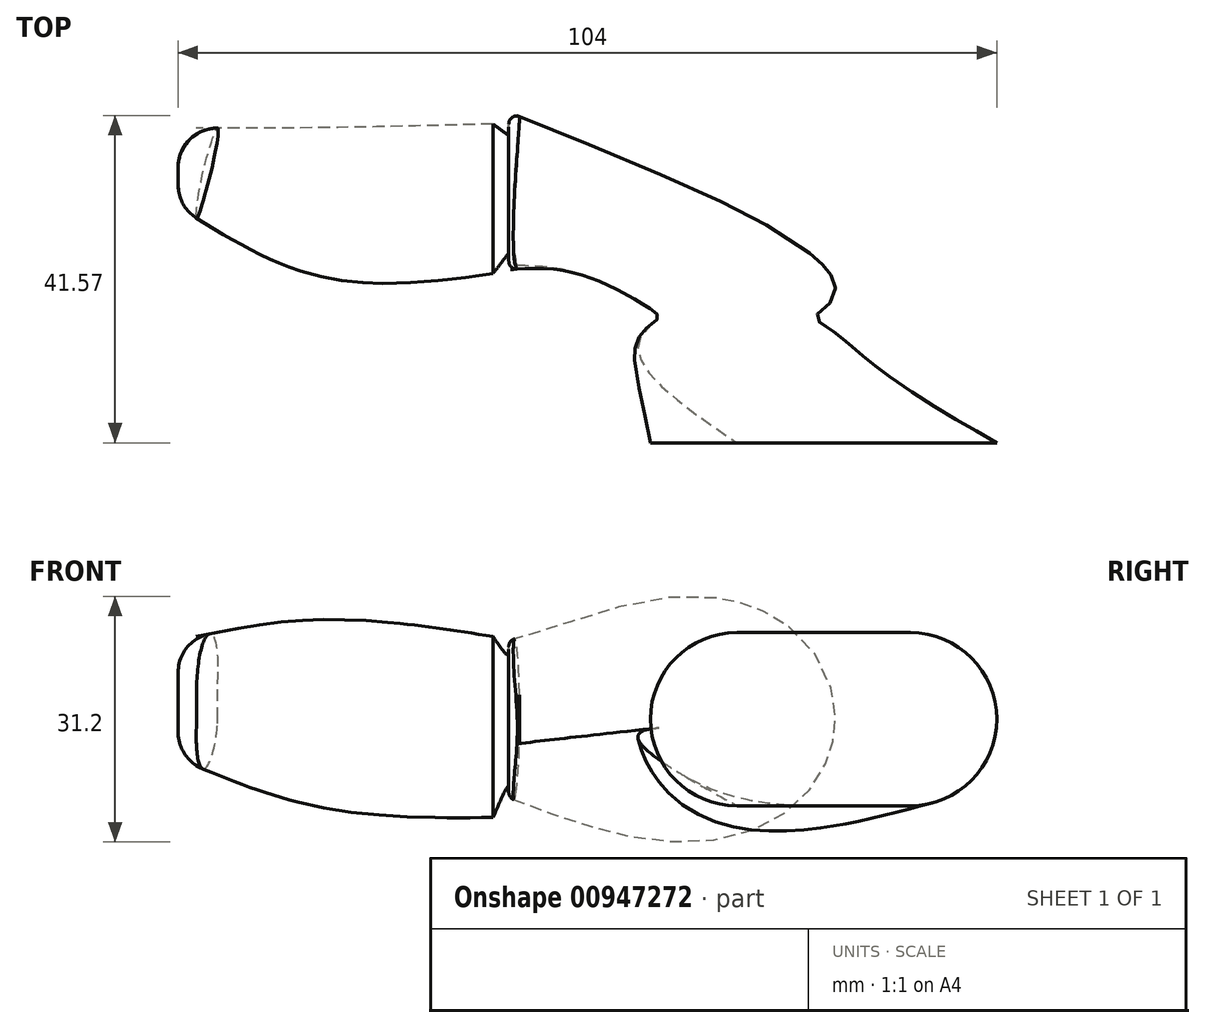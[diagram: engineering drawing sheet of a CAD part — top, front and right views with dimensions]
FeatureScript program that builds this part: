
annotation { "Feature Type Name" : "Feature", "Feature Type Description" : "" }
export const myFeature = defineFeature(function(context is Context, id is Id, definition is map)
    precondition{}
    {
        {
            var Q0;
            Q0=qCreatedBy(makeId("Front.planeOp"),FACE);
            cPlane(context, id + "F0", {"entities" : qUnion([Q0]), "cplaneType" : CPlaneType.OFFSET, "offset" : 15 * mm, "oppositeDirection" : true, "width" : 150 * mm, "height" : 150 * mm});
        }
        {
            var Q0;
            Q0=qCreatedBy(makeId("Front.planeOp"),FACE);
            var sketch = newSketch(context, id + "F1", { "sketchPlane" : qUnion([Q0])});
            skArc(sketch, "E0", {"start": v(11, -11) * mm, "mid": v(22, 0) * mm, "end": v(11, 11) * mm});
            skLineSegment(sketch, "E1", {"start": v(0, 30.33) * mm, "end": v(0, -39.22) * mm, "construction": true});
            skArc(sketch, "E2.MirrorC", {"start": v(-11, -11) * mm, "mid": v(-22, 0) * mm, "end": v(-11, 11) * mm});
            skLineSegment(sketch, "E3", {"start": v(11, 11) * mm, "end": v(-11, 11) * mm});
            skLineSegment(sketch, "E4", {"start": v(11, -11) * mm, "end": v(-11, -11) * mm});
            skSolve(sketch);
        }
        {
            var Q0;
            Q0=qCreatedBy(id+"F0.planeOp",FACE);
            var sketch = newSketch(context, id + "F2", { "sketchPlane" : qUnion([Q0])});
            skCircle(sketch, "E5", {"center": v(-11, 0) * mm, "radius": 11 * mm});
            skSolve(sketch);
        }
        {
            var Q0;
            Q0=qCreatedBy(id+"F0.planeOp",FACE);
            cPlane(context, id + "F3", {"entities" : qUnion([Q0]), "cplaneType" : CPlaneType.OFFSET, "offset" : 1 * mm, "oppositeDirection" : true, "width" : 150 * mm, "height" : 150 * mm});
        }
        {
            var Q0;
            Q0=qCreatedBy(id+"F3.planeOp",FACE);
            var sketch = newSketch(context, id + "F4", { "sketchPlane" : qUnion([Q0])});
            skCircle(sketch, "E6", {"center": v(-11, 0) * mm, "radius": 10 * mm});
            skSolve(sketch);
        }
        {
            var Q0;
            Q0=qCreatedBy(id+"F3.planeOp",FACE);
            cPlane(context, id + "F5", {"entities" : qUnion([Q0]), "cplaneType" : CPlaneType.OFFSET, "offset" : 1 * mm, "oppositeDirection" : true, "width" : 150 * mm, "height" : 150 * mm});
        }
        {
            var Q0;
            Q0=qCreatedBy(id+"F5.planeOp",FACE);
            var sketch = newSketch(context, id + "F6", { "sketchPlane" : qUnion([Q0])});
            skCircle(sketch, "E7", {"center": v(-11, 0) * mm, "radius": 11 * mm});
            skSolve(sketch);
        }
        {
            var Q0;
            Q0=qCreatedBy(makeId("Right.planeOp"),FACE);
            cPlane(context, id + "F7", {"entities" : qUnion([Q0]), "cplaneType" : CPlaneType.OFFSET, "offset" : 40 * mm, "oppositeDirection" : true, "width" : 150 * mm, "height" : 150 * mm});
        }
        {
            var Q0;
            Q0=qCreatedBy(id+"F7.planeOp",FACE);
            var sketch = newSketch(context, id + "F8", { "sketchPlane" : qUnion([Q0])});
            skCircle(sketch, "E8", {"center": v(32, 0) * mm, "radius": 10 * mm});
            skSolve(sketch);
        }
        {
            var Q0;
            Q0=makeQuery(id+"F8.imprint","IMPRINT",FACE,{"disambiguationData":[TD([[makeQuery(id+"F8.imprint","IMPRINT",EDGE,{"derivedFrom":sQuery(id+"F8.wireOp",EDGE,"E8")}),1.0]])]});
            var Q1;
            Q1=makeQuery(id+"F6.imprint","IMPRINT",FACE,{"disambiguationData":[TD([[makeQuery(id+"F6.imprint","IMPRINT",EDGE,{"derivedFrom":sQuery(id+"F6.wireOp",EDGE,"E7")}),1.0]])]});
            var Q2;
            Q2=makeQuery(id+"F4.imprint","IMPRINT",FACE,{"disambiguationData":[TD([[makeQuery(id+"F4.imprint","IMPRINT",EDGE,{"derivedFrom":sQuery(id+"F4.wireOp",EDGE,"E6")}),1.0]])]});
            var Q3;
            Q3=makeQuery(id+"F2.imprint","IMPRINT",FACE,{"disambiguationData":[TD([[makeQuery(id+"F2.imprint","IMPRINT",EDGE,{"derivedFrom":sQuery(id+"F2.wireOp",EDGE,"E5")}),1.0]])]});
            var Q4;
            Q4=makeQuery(id+"F1.imprint","IMPRINT",FACE,{"disambiguationData":[TD([[makeQuery(id+"F1.imprint","IMPRINT",EDGE,{"derivedFrom":sQuery(id+"F1.wireOp",EDGE,"E0")}),1.0]])]});
            loft(context, id + "F9", {"sheetProfilesArray" : [{ "sheetProfileEntities" : qUnion([Q0]) }, { "sheetProfileEntities" : qUnion([Q1]) }, { "sheetProfileEntities" : qUnion([Q2]) }, { "sheetProfileEntities" : qUnion([Q3]) }, { "sheetProfileEntities" : qUnion([Q4]) }]});
        }
        {
            var Q0;
            Q0=makeQuery(id+"F9.opLoft","CAP_FACE",FACE,{"disambiguationData":[OSD([makeQuery(id+"F8.imprint","IMPRINT",FACE,{"disambiguationData":[TD([[makeQuery(id+"F8.imprint","IMPRINT",EDGE,{"derivedFrom":sQuery(id+"F8.wireOp",EDGE,"E8")}),1.0]])]})])],"isStart":true});
            fillet(context, id + "F10", {"entities" : qUnion([Q0]), "tangentPropagation" : true, "radius" : 1 * mm, "defaultsChanged" : true, "vertexSettings" : [], "allowEdgeOverflow" : false});
        }
        {
            var Q0;
            Q0=makeQuery(id+"F9.opLoft","CAP_FACE",FACE,{"disambiguationData":[OSD([makeQuery(id+"F8.imprint","IMPRINT",FACE,{"disambiguationData":[TD([[makeQuery(id+"F8.imprint","IMPRINT",EDGE,{"derivedFrom":sQuery(id+"F8.wireOp",EDGE,"E8")}),1.0]])]})])],"isStart":true});
            var sketch = newSketch(context, id + "F11", { "sketchPlane" : qUnion([Q0])});
            skFitSpline(sketch, "E9.0", {"points": [v(-29.1, 8.18) * mm, v(-29.6, 8.33) * mm, v(-30.63, 8.52) * mm, v(-31.94, 8.48) * mm, v(-32.97, 8.27) * mm, v(-33.7, 8.04) * mm, v(-34.42, 7.73) * mm, v(-35.1, 7.35) * mm, v(-35.74, 6.9) * mm, v(-36.33, 6.4) * mm, v(-36.87, 5.82) * mm, v(-37.35, 5.21) * mm, v(-37.78, 4.56) * mm, v(-38.14, 3.88) * mm, v(-38.45, 3.15) * mm, v(-38.62, 2.66) * mm, v(-38.69, 2.4) * mm]});
            skFitSpline(sketch, "E9.1", {"points": [v(-38.69, 2.4) * mm, v(-38.83, 1.92) * mm, v(-38.97, 1.18) * mm, v(-39.04, 0.18) * mm, v(-39.04, -0.59) * mm, v(-38.97, -1.34) * mm, v(-38.85, -2.08) * mm, v(-38.66, -2.8) * mm, v(-38.41, -3.53) * mm, v(-38.1, -4.22) * mm, v(-37.75, -4.87) * mm, v(-37.33, -5.5) * mm, v(-36.85, -6.09) * mm, v(-36.32, -6.63) * mm, v(-35.56, -7.28) * mm, v(-34.92, -7.68) * mm, v(-34.46, -7.9) * mm]});
            skFitSpline(sketch, "E9.2", {"points": [v(-34.46, -7.9) * mm, v(-33.97, -8.13) * mm, v(-33.21, -8.4) * mm, v(-32.14, -8.58) * mm, v(-31.33, -8.62) * mm, v(-30.52, -8.57) * mm, v(-29.72, -8.43) * mm, v(-28.94, -8.2) * mm, v(-28.2, -7.88) * mm, v(-27.61, -7.54) * mm, v(-27.17, -7.22) * mm, v(-26.75, -6.88) * mm, v(-26.36, -6.5) * mm, v(-26.02, -6.09) * mm, v(-25.7, -5.65) * mm, v(-25.35, -5.06) * mm, v(-25.02, -4.33) * mm, v(-24.75, -3.56) * mm, v(-24.61, -3.03) * mm, v(-24.55, -2.77) * mm]});
            skFitSpline(sketch, "E9.3", {"points": [v(-24.55, -2.77) * mm, v(-24.42, -2.23) * mm, v(-24.24, -1.14) * mm, v(-24.13, 0.23) * mm, v(-24.12, 1.33) * mm, v(-24.18, 2.44) * mm, v(-24.37, 3.52) * mm, v(-24.77, 4.57) * mm, v(-25.17, 5.29) * mm, v(-25.66, 5.95) * mm, v(-26.24, 6.56) * mm, v(-26.87, 7.09) * mm, v(-27.57, 7.54) * mm, v(-28.32, 7.91) * mm, v(-28.84, 8.1) * mm, v(-29.1, 8.18) * mm]});
            skSolve(sketch);
        }
        {
            var Q0;
            Q0=qCreatedBy(id+"F7.planeOp",FACE);
            cPlane(context, id + "F12", {"entities" : qUnion([Q0]), "cplaneType" : CPlaneType.OFFSET, "offset" : 2 * mm, "oppositeDirection" : true, "width" : 150 * mm, "height" : 150 * mm});
        }
        {
            var Q0;
            Q0=qCreatedBy(id+"F12.planeOp",FACE);
            var sketch = newSketch(context, id + "F13", { "sketchPlane" : qUnion([Q0])});
            skArc(sketch, "E10", {"start": v(21.5, -3) * mm, "mid": v(31, -12.5) * mm, "end": v(40.5, -3) * mm});
            skArc(sketch, "E11", {"start": v(40.5, 1) * mm, "mid": v(31, 10.5) * mm, "end": v(21.5, 1) * mm});
            skLineSegment(sketch, "E12", {"start": v(40.5, 1) * mm, "end": v(40.5, -3) * mm});
            skLineSegment(sketch, "E13", {"start": v(21.5, -3) * mm, "end": v(21.5, 1) * mm});
            skSolve(sketch);
        }
        {
            var Q0;
            Q0 = qSketchRegion(id + "F11", true);
            var Q1;
            Q1 = qSketchRegion(id + "F13", true);
            loft(context, id + "F14", {"operationType" : NewBodyOperationType.ADD, "sheetProfilesArray" : [{ "sheetProfileEntities" : qUnion([Q0]) }, { "sheetProfileEntities" : qUnion([Q1]) }]});
        }
        {
            var Q0;
            Q0=makeQuery(id+"F13.imprint","IMPRINT",FACE,{"disambiguationData":[TD([[makeQuery(id+"F13.imprint","IMPRINT",EDGE,{"derivedFrom":sQuery(id+"F13.wireOp",EDGE,"E10")}),1.0]])]});
            var sketch = newSketch(context, id + "F15", { "sketchPlane" : qUnion([Q0])});
            skArc(sketch, "E14.0", {"start": v(40.5, 1) * mm, "mid": v(31, 10.5) * mm, "end": v(21.5, 1) * mm});
            skArc(sketch, "E14.1", {"start": v(21.5, -3) * mm, "mid": v(31, -12.5) * mm, "end": v(40.5, -3) * mm});
            skLineSegment(sketch, "E14.2", {"start": v(21.5, -3) * mm, "end": v(21.5, 1) * mm});
            skLineSegment(sketch, "E14.3", {"start": v(40.5, 1) * mm, "end": v(40.5, -3) * mm});
            skSolve(sketch);
        }
        {
            var Q0;
            Q0=qCreatedBy(id+"F12.planeOp",FACE);
            cPlane(context, id + "F16", {"entities" : qUnion([Q0]), "cplaneType" : CPlaneType.OFFSET, "offset" : 25 * mm, "oppositeDirection" : true, "width" : 150 * mm, "height" : 150 * mm});
        }
        {
            var Q0;
            Q0=qCreatedBy(id+"F16.planeOp",FACE);
            var sketch = newSketch(context, id + "F17", { "sketchPlane" : qUnion([Q0])});
            skArc(sketch, "E15", {"start": v(40, 3.5) * mm, "mid": v(31, 12.5) * mm, "end": v(22, 3.5) * mm});
            skArc(sketch, "E16", {"start": v(22, -1.5) * mm, "mid": v(31, -10.5) * mm, "end": v(40, -1.5) * mm});
            skLineSegment(sketch, "E17", {"start": v(40, -1.5) * mm, "end": v(40, 3.5) * mm});
            skLineSegment(sketch, "E18", {"start": v(22, -1.5) * mm, "end": v(22, 3.5) * mm});
            skSolve(sketch);
        }
        {
            var Q0;
            Q0=qCreatedBy(id+"F16.planeOp",FACE);
            cPlane(context, id + "F18", {"entities" : qUnion([Q0]), "cplaneType" : CPlaneType.OFFSET, "offset" : 15 * mm, "oppositeDirection" : true, "width" : 150 * mm, "height" : 150 * mm});
        }
        {
            var Q0;
            Q0=qCreatedBy(id+"F18.planeOp",FACE);
            var sketch = newSketch(context, id + "F19", { "sketchPlane" : qUnion([Q0])});
            skArc(sketch, "E19", {"start": v(40, 5) * mm, "mid": v(35, 10) * mm, "end": v(30, 5) * mm});
            skArc(sketch, "E20", {"start": v(30, 0) * mm, "mid": v(35, -5) * mm, "end": v(40, 0) * mm});
            skLineSegment(sketch, "E21", {"start": v(40, 0) * mm, "end": v(40, 5) * mm});
            skLineSegment(sketch, "E22", {"start": v(30, 0) * mm, "end": v(30, 5) * mm});
            skSolve(sketch);
        }
        {
            var Q0;
            Q0 = qSketchRegion(id + "F15", true);
            var Q1;
            Q1 = qSketchRegion(id + "F17", true);
            var Q2;
            Q2 = qSketchRegion(id + "F19", true);
            loft(context, id + "F20", {"operationType" : NewBodyOperationType.ADD, "sheetProfilesArray" : [{ "sheetProfileEntities" : qUnion([Q0]) }, { "sheetProfileEntities" : qUnion([Q1]) }, { "sheetProfileEntities" : qUnion([Q2]) }]});
        }
        {
            var Q0;
            Q0=makeQuery(id+"F20.opLoft","CAP_FACE",FACE,{"disambiguationData":[OSD([makeQuery(id+"F19.imprint","IMPRINT",FACE,{"disambiguationData":[TD([[makeQuery(id+"F19.imprint","IMPRINT",EDGE,{"derivedFrom":sQuery(id+"F19.wireOp",EDGE,"E19")}),1.0]])]})])],"isStart":true});
            fillet(context, id + "F21", {"entities" : qUnion([Q0]), "tangentPropagation" : true, "radius" : 5 * mm, "defaultsChanged" : false, "vertexSettings" : [], "allowEdgeOverflow" : false});
        }
    });
